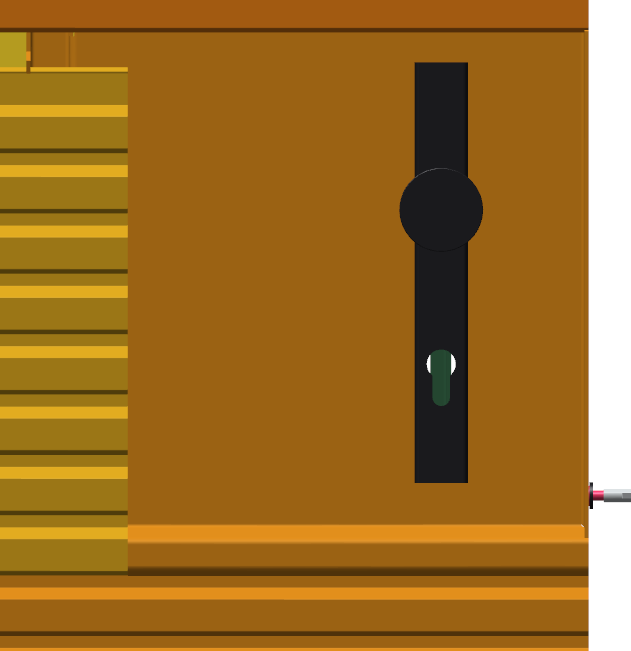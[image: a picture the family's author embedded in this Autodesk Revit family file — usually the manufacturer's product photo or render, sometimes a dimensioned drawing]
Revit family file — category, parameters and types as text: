
# Revit family: NLRS_31_DO_WB_HJ44 enkele deur-AV_jazo_jazo
name_source: partatom
category: Doors
units: mm (PartAtom-declared; Revit-internal decimal feet)

## family parameters
Always vertical = Yes
Cut with Voids When Loaded = No
Host = Wall
OmniClass Number = 23.30.10.00
OmniClass Title = Doors
Room Calculation Point = No
Shared = No

## types (1)
- TYPE CATALOG
    Analytic Construction = <None>
    Assembly Code = 23.30.10.00
    Construction Type = Voor specificaties of mogelijkheden, neem contact op.
    Define Thermal Properties by = User Defined
    Description = HJ44 enkele deur
    Function = Exterior
    Height = 2000 mm  [stored 6.56168 ft]
    JAZO_C_aluminium kozijn = No
    JAZO_C_calculatie_01 = 37 mm  [stored 0.121391 ft]
    JAZO_C_calculatie_02 = 565 mm
    JAZO_C_calculatie_03 = -59 mm
    JAZO_C_dagmaat breedte = 860 mm
    JAZO_C_dagmaat hoogte = 1860 mm  [stored 6.10236 ft]
    JAZO_C_forster presto kozijn = Yes
    JAZO_C_materiaal aluminium kozijn = <By Category>
    JAZO_C_materiaal aluminium planken = <By Category>
    JAZO_C_materiaal beslag = <By Category>
    JAZO_C_materiaal forster presto deurprofiel = <By Category>
    JAZO_C_materiaal forster presto kozijn = <By Category>
    JAZO_C_materiaal forster presto sandwichpaneel = <By Category>
    JAZO_C_materiaal scharnier = <By Category>
    JAZO_C_materiaal schoep = <By Category>
    JAZO_C_niet ventilerend = Yes
    JAZO_C_opbouwrooster HJ44 = Yes
    JAZO_C_paniekfunctie = No
    JAZO_C_ventilerend = No
    MAX HEIGHT = 3000 mm  [stored 9.84252 ft]
    MAX WIDTH = 1500 mm  [stored 4.92126 ft]
    MIN HEIGHT = 1850 mm  [stored 6.06955 ft]
    MIN WIDTH = 850 mm  [stored 2.78871 ft]
    Manufacturer = JAZO Zevenaar bv
    Model = HJ44 enkele deur
    NLRS_C_aantal_01 = 2
    NLRS_C_aantal_02 = 11
    NLRS_C_brandwerend = No
    NLRS_C_breedte = 1000 mm  [stored 3.28084 ft]
    NLRS_C_breedte_01 = 1010 mm  [stored 3.31365 ft]
    NLRS_C_breedte_max = 1500 mm  [stored 4.92126 ft]
    NLRS_C_breedte_min = 850 mm  [stored 2.78871 ft]
    NLRS_C_content_datum gewijzigd = 7-11-2022
    NLRS_C_content_datum uitgifte = 17-8-2022
    NLRS_C_content_provider = JAZO Zevenaar bv
    NLRS_C_content_revit versie = REVIT 2020.2
    NLRS_C_content_versie = 2.5
    NLRS_C_diepte = 50 mm  [stored 0.164042 ft]
    NLRS_C_diepte_01 = 111 mm
    NLRS_C_diepte_02 = 50 mm  [stored 0.164042 ft]
    NLRS_C_geluidwering Rw = Voor specificaties of mogelijkheden, neem contact op.
    NLRS_C_hoogte = 2000 mm  [stored 6.56168 ft]
    NLRS_C_hoogte_01 = 2010 mm  [stored 6.59449 ft]
    NLRS_C_hoogte_max = 3000 mm  [stored 9.84252 ft]
    NLRS_C_hoogte_min = 1850 mm  [stored 6.06955 ft]
    NLRS_C_inbraakwerend = No
    NLRS_C_lengte_01 = 96 mm  [stored 0.314961 ft]
    NLRS_C_lengte_02 = 565 mm
    NLRS_C_leverancier_adres = Handelsdwarsstraat 10
    NLRS_C_leverancier_bedrijfsnaam = JAZO Zevenaar bv
    NLRS_C_leverancier_plaats = Zevenaar
    NLRS_C_leverancier_postcode = 6905 DJ
    NLRS_C_leverancier_telefoonnummer = +31 316 - 59 29 11
    NLRS_C_leverancier_url = www.jazo.com
    NLRS_C_merk = Voor specificaties of mogelijkheden, neem contact op.
    NLRS_C_offset = 61 mm  [stored 0.200131 ft]
    NLRS_C_offset_01 = 0 mm  [stored 0 ft]
    NLRS_C_offset_02 = 37 mm  [stored 0.121391 ft]
    NLRS_C_rookwerendheid = Voor specificaties of mogelijkheden, neem contact op.
    NLRS_C_stelruimte = 5 mm  [stored 0.0164042 ft]
    NLRS_C_vluchtroute = Voor specificaties of mogelijkheden, neem contact op.
    NLRS_C_weerstandsklasse = Voor specificaties of mogelijkheden, neem contact op.
    NLRS_C_zelfsluitend = No
    Negge = 61 mm  [stored 0.200131 ft]
    Rough Height = 2010 mm  [stored 6.59449 ft]
    Rough Width = 1010 mm  [stored 3.31365 ft]
    Thickness = 50 mm  [stored 0.164042 ft]
    URL = www.jazo.com
    Wall Closure = By host
    Width = 1000 mm  [stored 3.28084 ft]

note: [stored X ft] marks values corroborated as IEEE doubles in the binary element streams (Revit-internal decimal feet)

## geometry (parser evidence)
native form markers: Sweep x53
no freeform markers — native parametric forms only
